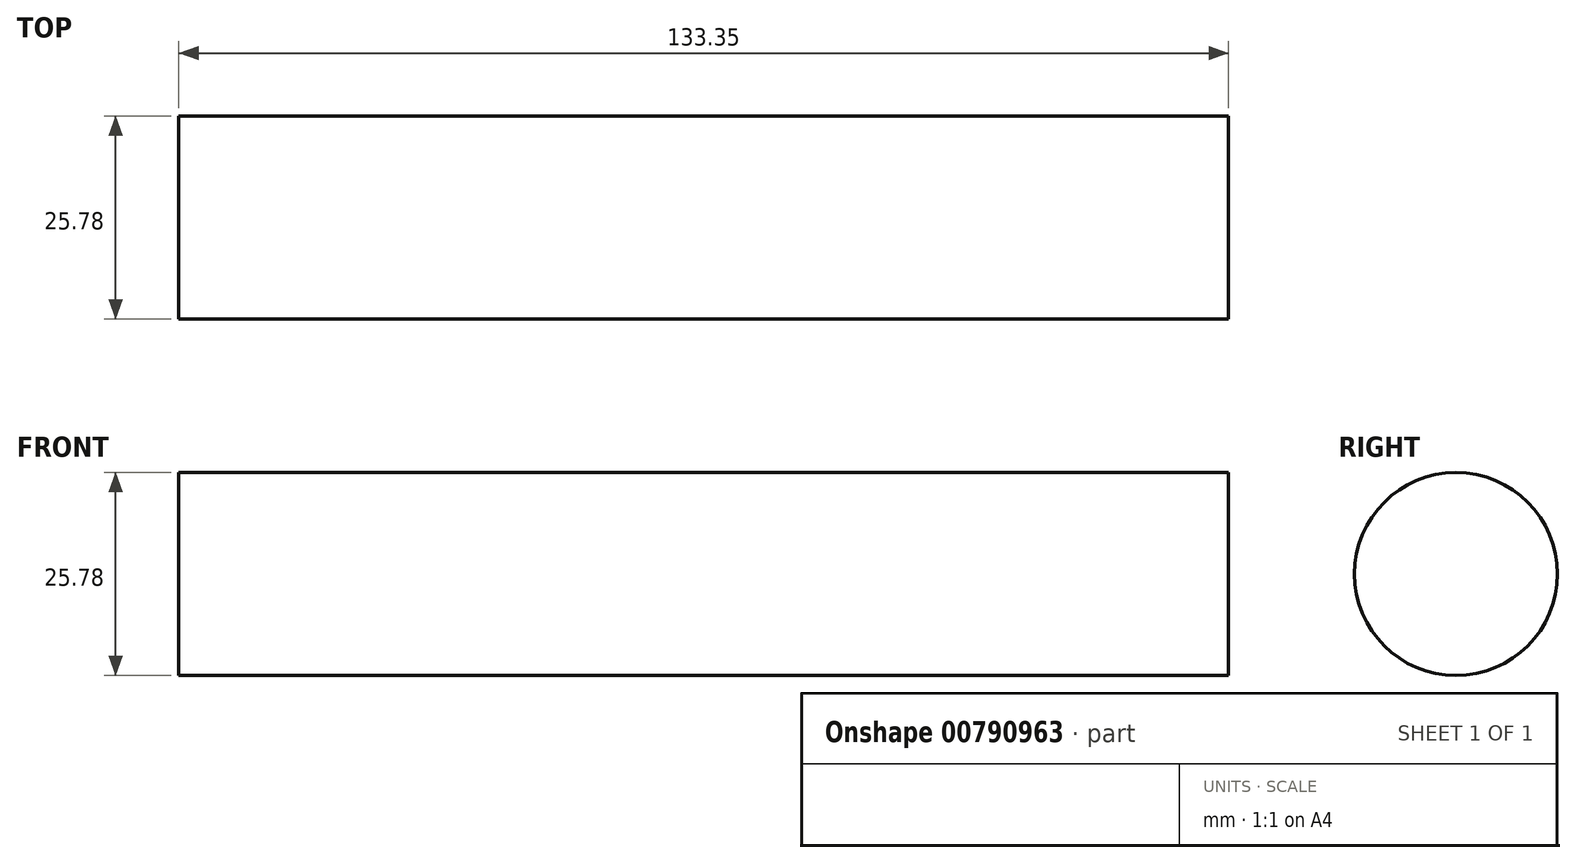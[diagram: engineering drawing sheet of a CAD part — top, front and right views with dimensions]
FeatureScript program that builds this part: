
annotation { "Feature Type Name" : "Feature", "Feature Type Description" : "" }
export const myFeature = defineFeature(function(context is Context, id is Id, definition is map)
    precondition{}
    {
        {
            var Q0;
            Q0=qCreatedBy(makeId("Right.planeOp"),FACE);
            var sketch = newSketch(context, id + "F0", { "sketchPlane" : qUnion([Q0])});
            skCircle(sketch, "E0", {"center": v(0, 0) * mm, "radius": 12.89 * mm});
            skSolve(sketch);
        }
        {
            var Q0;
            Q0 = qSketchRegion(id + "F0", true);
            extrude(context, id + "F1", {"entities" : qUnion([Q0]), "oppositeDirection" : true, "depth" : 133.35 * mm, "offsetDistance" : 25.4 * mm});
        }
    });
